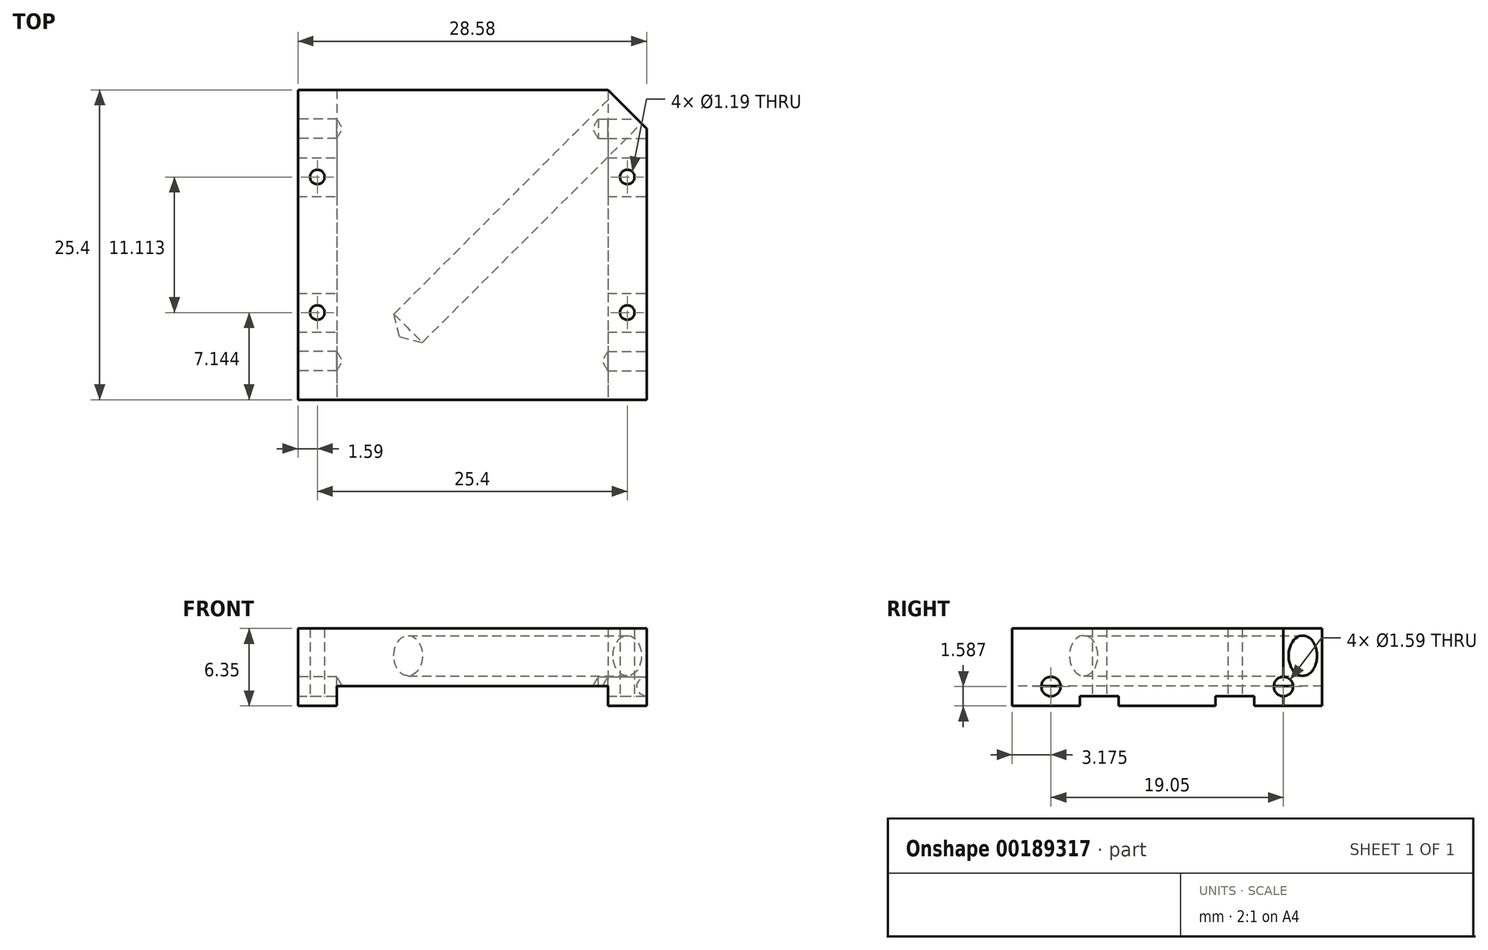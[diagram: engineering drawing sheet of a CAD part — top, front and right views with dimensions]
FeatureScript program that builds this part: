
annotation { "Feature Type Name" : "Feature", "Feature Type Description" : "" }
export const myFeature = defineFeature(function(context is Context, id is Id, definition is map)
    precondition{}
    {
        {
            var Q0;
            Q0=qCreatedBy(makeId("Top.planeOp"),FACE);
            var sketch = newSketch(context, id + "F0", { "sketchPlane" : qUnion([Q0])});
            skLineSegment(sketch, "E0.bottom", {"start": v(11.11, 12.7) * mm, "end": v(-14.29, 12.7) * mm});
            skLineSegment(sketch, "E0.top", {"start": v(14.29, -12.7) * mm, "end": v(-14.29, -12.7) * mm});
            skLineSegment(sketch, "E0.left", {"start": v(14.29, 9.53) * mm, "end": v(14.29, -12.7) * mm});
            skLineSegment(sketch, "E0.right", {"start": v(-14.29, 12.7) * mm, "end": v(-14.29, -12.7) * mm});
            skLineSegment(sketch, "E1", {"start": v(11.11, 12.7) * mm, "end": v(14.29, 9.53) * mm});
            skPoint(sketch, "E2.orphan", {"position": v(14.29, 12.7) * mm});
            skSolve(sketch);
        }
        {
            var Q0;
            Q0=makeQuery(id+"F0.imprint","IMPRINT",FACE,{"disambiguationData":[TD([[makeQuery(id+"F0.imprint","IMPRINT",EDGE,{"derivedFrom":sQuery(id+"F0.wireOp",EDGE,"E0.bottom")}),1.0]])]});
            extrude(context, id + "F1", {"entities" : qUnion([Q0]), "depth" : 6.35 * mm});
        }
        {
            var Q0;
            Q0=makeQuery(id+"F1.opExtrude","SWEPT_FACE",FACE,{"disambiguationData":[OSD([sQuery(id+"F0.wireOp",EDGE,"E0.right")])]});
            var sketch = newSketch(context, id + "F2", { "sketchPlane" : qUnion([Q0])});
            skCircle(sketch, "E3", {"center": v(-9.52, 1.59) * mm, "radius": 0.8 * mm});
            skCircle(sketch, "E4.1.0.0", {"center": v(9.53, 1.59) * mm, "radius": 0.8 * mm});
            skLineSegment(sketch, "E4.direction1", {"start": v(-9.52, 1.59) * mm, "end": v(9.53, 1.59) * mm, "construction": true});
            skSolve(sketch);
        }
        {
            var Q0;
            Q0=sQuery(id+"F2.wireOp",VERTEX,"E3.center");
            var Q1;
            Q1=sQuery(id+"F2.wireOp",VERTEX,"E4.1.0.0.center");
            var Q2;
            Q2=makeQuery(id+"F1.opExtrude","SWEPT_BODY",BODY,{"disambiguationData":[OSD([sQuery(id+"F0.wireOp",EDGE,"E0.bottom"),sQuery(id+"F0.wireOp",EDGE,"E0.top"),sQuery(id+"F0.wireOp",EDGE,"E0.left"),sQuery(id+"F0.wireOp",EDGE,"E0.right")])]});
            hole(context, id + "F3", {"style" : HoleStyle.SIMPLE, "endStyle" : HoleEndStyle.BLIND, "holeDiameter" : 1.59 * mm, "holeDepth" : 3.17 * mm, "locations" : qUnion([Q0, Q1]), "scope" : qUnion([Q2])});
        }
        {
            var Q0;
            Q0=makeQuery(id+"F1.opExtrude","SWEPT_FACE",FACE,{"disambiguationData":[OSD([sQuery(id+"F0.wireOp",EDGE,"E0.left")])]});
            var sketch = newSketch(context, id + "F4", { "sketchPlane" : qUnion([Q0])});
            skPoint(sketch, "E5", {"position": v(-9.53, 1.59) * mm});
            skPoint(sketch, "E6.1.0.0", {"position": v(9.52, 1.59) * mm});
            skLineSegment(sketch, "E6.direction1", {"start": v(-9.53, 1.59) * mm, "end": v(9.52, 1.59) * mm, "construction": true});
            skSolve(sketch);
        }
        {
            var Q0;
            Q0=sQuery(id+"F4.wireOp",VERTEX,"E5");
            var Q1;
            Q1=sQuery(id+"F4.wireOp",VERTEX,"E6.1.0.0");
            var Q2;
            Q2=makeQuery(id+"F1.opExtrude","SWEPT_BODY",BODY,{"disambiguationData":[OSD([sQuery(id+"F0.wireOp",EDGE,"E0.bottom"),sQuery(id+"F0.wireOp",EDGE,"E0.top"),sQuery(id+"F0.wireOp",EDGE,"E0.left"),sQuery(id+"F0.wireOp",EDGE,"E0.right")])]});
            hole(context, id + "F5", {"style" : HoleStyle.SIMPLE, "endStyle" : HoleEndStyle.BLIND, "holeDiameter" : 1.59 * mm, "holeDepth" : 3.17 * mm, "locations" : qUnion([Q0, Q1]), "scope" : qUnion([Q2])});
        }
        {
            var Q0;
            Q0=makeQuery(id+"F1.opExtrude","SWEPT_FACE",FACE,{"disambiguationData":[OSD([sQuery(id+"F0.wireOp",EDGE,"E0.top")])]});
            var sketch = newSketch(context, id + "F6", { "sketchPlane" : qUnion([Q0])});
            skLineSegment(sketch, "E7.bottom", {"start": v(-11.11, 0) * mm, "end": v(11.11, 0) * mm});
            skLineSegment(sketch, "E7.top", {"start": v(-11.11, 1.64) * mm, "end": v(11.11, 1.64) * mm});
            skLineSegment(sketch, "E7.left", {"start": v(-11.11, 0) * mm, "end": v(-11.11, 1.64) * mm});
            skLineSegment(sketch, "E7.right", {"start": v(11.11, 0) * mm, "end": v(11.11, 1.64) * mm});
            skSolve(sketch);
        }
        {
            var Q0;
            Q0 = qSketchRegion(id + "F6", true);
            extrude(context, id + "F7", {"entities" : qUnion([Q0]), "operationType" : NewBodyOperationType.REMOVE, "endBound" : BoundingType.THROUGH_ALL, "oppositeDirection" : true, "depth" : 25.4 * mm});
        }
        {
            var Q0;
            {var subQ0=sQuery(id+"F0.wireOp",EDGE,"E0.bottom");var subQ1=sQuery(id+"F0.wireOp",EDGE,"E0.top");var subQ2=sQuery(id+"F0.wireOp",EDGE,"E0.right");Q0=makeQuery(id+"F7.boolean.opBoolean","SPLIT",FACE,{"disambiguationData":[TD([makeQuery(id+"F1.opExtrude","SWEPT_FACE",FACE,{"disambiguationData":[OSD([subQ2])]})])],"derivedFrom":makeQuery(id+"F1.opExtrude","CAP_FACE",FACE,{"disambiguationData":[OSD([subQ0,subQ1,sQuery(id+"F0.wireOp",EDGE,"E0.left"),subQ2])],"isStart":true})});}
            var sketch = newSketch(context, id + "F8", { "sketchPlane" : qUnion([Q0])});
            skLineSegment(sketch, "E8", {"start": v(-14.29, 3.97) * mm, "end": v(-11.11, 3.97) * mm});
            skLineSegment(sketch, "E9.0", {"start": v(-14.29, 7.14) * mm, "end": v(-11.11, 7.14) * mm});
            skLineSegment(sketch, "E10.MirrorCS", {"start": v(-14.29, -3.97) * mm, "end": v(-11.11, -3.97) * mm});
            skLineSegment(sketch, "E11.MirrorCS", {"start": v(-14.29, -7.14) * mm, "end": v(-11.11, -7.14) * mm});
            skPoint(sketch, "E12", {"position": v(-12.7, 5.56) * mm});
            skPoint(sketch, "E13.MirrorP", {"position": v(-12.7, -5.56) * mm});
            skSolve(sketch);
        }
        {
            var Q0;
            {var subQ0=sQuery(id+"F0.wireOp",EDGE,"E0.bottom");var subQ1=sQuery(id+"F0.wireOp",EDGE,"E0.top");var subQ2=sQuery(id+"F0.wireOp",EDGE,"E0.left");Q0=makeQuery(id+"F7.boolean.opBoolean","SPLIT",FACE,{"disambiguationData":[TD([makeQuery(id+"F1.opExtrude","SWEPT_FACE",FACE,{"disambiguationData":[OSD([subQ2])]})])],"derivedFrom":makeQuery(id+"F1.opExtrude","CAP_FACE",FACE,{"disambiguationData":[OSD([subQ0,subQ1,subQ2,sQuery(id+"F0.wireOp",EDGE,"E0.right")])],"isStart":true})});}
            var sketch = newSketch(context, id + "F9", { "sketchPlane" : qUnion([Q0])});
            skLineSegment(sketch, "E14", {"start": v(11.11, 3.97) * mm, "end": v(14.29, 3.97) * mm});
            skLineSegment(sketch, "E15.0", {"start": v(11.11, 7.14) * mm, "end": v(14.29, 7.14) * mm});
            skLineSegment(sketch, "E16.MirrorCS", {"start": v(11.11, -7.14) * mm, "end": v(14.29, -7.14) * mm});
            skLineSegment(sketch, "E17.MirrorCS", {"start": v(11.11, -3.97) * mm, "end": v(14.29, -3.97) * mm});
            skPoint(sketch, "E18", {"position": v(12.7, 5.56) * mm});
            skPoint(sketch, "E19.MirrorP", {"position": v(12.7, -5.56) * mm});
            skSolve(sketch);
        }
        {
            var Q0;
            {var subQ0=sQuery(id+"F8.wireOp",EDGE,"E8");Q0=makeQuery(id+"F8.imprint","IMPRINT",FACE,{"disambiguationData":[TD([[makeQuery(id+"F8.imprint","IMPRINT",EDGE,{"derivedFrom":subQ0}),1.0]])]});}
            var Q1;
            {var subQ0=sQuery(id+"F8.wireOp",EDGE,"E10.MirrorCS");Q1=makeQuery(id+"F8.imprint","IMPRINT",FACE,{"disambiguationData":[TD([[makeQuery(id+"F8.imprint","IMPRINT",EDGE,{"derivedFrom":subQ0}),-1.0]])]});}
            var Q2;
            {var subQ0=sQuery(id+"F9.wireOp",EDGE,"E16.MirrorCS");Q2=makeQuery(id+"F9.imprint","IMPRINT",FACE,{"disambiguationData":[TD([[makeQuery(id+"F9.imprint","IMPRINT",EDGE,{"derivedFrom":subQ0}),1.0]])]});}
            var Q3;
            {var subQ0=sQuery(id+"F9.wireOp",EDGE,"E14");Q3=makeQuery(id+"F9.imprint","IMPRINT",FACE,{"disambiguationData":[TD([[makeQuery(id+"F9.imprint","IMPRINT",EDGE,{"derivedFrom":subQ0}),1.0]])]});}
            extrude(context, id + "F10", {"entities" : qUnion([Q0, Q1, Q2, Q3]), "operationType" : NewBodyOperationType.REMOVE, "oppositeDirection" : true, "depth" : 0.8 * mm});
        }
        {
            var Q0;
            Q0=sQuery(id+"F8.wireOp",VERTEX,"E12");
            var Q1;
            Q1=sQuery(id+"F8.wireOp",VERTEX,"E13.MirrorP");
            var Q2;
            Q2=sQuery(id+"F9.wireOp",VERTEX,"E18");
            var Q3;
            Q3=sQuery(id+"F9.wireOp",VERTEX,"E19.MirrorP");
            var Q4;
            Q4=makeQuery(id+"F1.opExtrude","SWEPT_BODY",BODY,{"disambiguationData":[OSD([sQuery(id+"F0.wireOp",EDGE,"E0.bottom"),sQuery(id+"F0.wireOp",EDGE,"E0.top"),sQuery(id+"F0.wireOp",EDGE,"E0.left"),sQuery(id+"F0.wireOp",EDGE,"E0.right")])]});
            hole(context, id + "F11", {"style" : HoleStyle.SIMPLE, "endStyle" : HoleEndStyle.THROUGH, "standardTappedOrClearance" : lookupTablePath({ "standard" : "ANSI", "engagement" : "75%", "pitch" : "80 tpi", "size" : "#0", "type" : "Tapped" }), "standardBlindInLast" : lookupTablePath({ "standard" : "ANSI", "engagement" : "75%", "pitch" : "80 tpi", "size" : "#0", "type" : "Tapped" }), "holeDiameter" : 1.2 * mm, "locations" : qUnion([Q0, Q1, Q2, Q3]), "scope" : qUnion([Q4]), "isTappedThrough" : true, "majorDiameter" : 1.52 * mm, "showTappedDepth" : true});
        }
        {
            var Q0;
            Q0=makeQuery(id+"F1.opExtrude","SWEPT_FACE",FACE,{"disambiguationData":[OSD([sQuery(id+"F0.wireOp",EDGE,"E1")])]});
            var sketch = newSketch(context, id + "F12", { "sketchPlane" : qUnion([Q0])});
            skLineSegment(sketch, "E20", {"start": v(-1.12, 6.35) * mm, "end": v(-1.12, 4.11) * mm});
            skPoint(sketch, "E21", {"position": v(-1.12, 4.11) * mm});
            skSolve(sketch);
        }
        {
            var Q0;
            Q0=sQuery(id+"F12.wireOp",VERTEX,"E21");
            var Q1;
            Q1=makeQuery(id+"F1.opExtrude","SWEPT_BODY",BODY,{"disambiguationData":[OSD([sQuery(id+"F0.wireOp",EDGE,"E0.bottom"),sQuery(id+"F0.wireOp",EDGE,"E0.top"),sQuery(id+"F0.wireOp",EDGE,"E0.left"),sQuery(id+"F0.wireOp",EDGE,"E0.right"),sQuery(id+"F0.wireOp",EDGE,"E1")])]});
            hole(context, id + "F13", {"style" : HoleStyle.SIMPLE, "endStyle" : HoleEndStyle.BLIND, "holeDiameter" : 3.3 * mm, "holeDepth" : 25.4 * mm, "locations" : qUnion([Q0]), "scope" : qUnion([Q1])});
        }
    });
